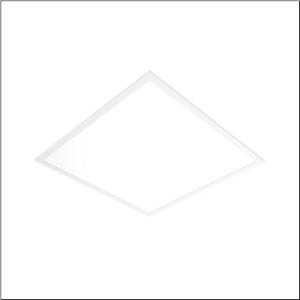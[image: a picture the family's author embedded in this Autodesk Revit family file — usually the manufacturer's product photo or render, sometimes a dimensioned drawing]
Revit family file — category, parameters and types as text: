
# Revit family: apollon_r__41_51mh11w72343_11b4
name_source: partatom
category: Lighting Fixtures
units: mm (PartAtom-declared; Revit-internal decimal feet)

## family parameters
Cut with Voids When Loaded = No
Host = Face
Light Source = No
Part Type = Normal
Room Calculation Point = No
Round Connector Dimension = Use Diameter
Shared = No

## types (1)
- Apollon® 41 (1 x LED, 3500 lm, 28.5 W, 3000K)
    Apparent Load = 29 VA
    CIE Flux Codes = 61 87 97 100 100
    Color Rendering = 80
    Color Temperature = 3000K
    Default Elevation = 1800 mm
    Description = Apollon® 41, office luminaire, primary optical cover: prismatic diffuser, of PS, light emission: direct distribution, primary light characteristic: symmetric, installation type: lay-in mounting, LED, rated luminous flux: 3.500lm, luminous efficacy: 123lm/W, light colour: 830, colour temperature: 3000K, with terminal, 3-pole, mains connection: 220..240V, AC, 50/60Hz, housing, of aluminium section, traffic white (RAL 9016), module: M625, length: 620mm, width: 620mm, height: 40mm, housing upper side, of sheet steel, protection rating (complete): IP20, protection rating (lamp compartment, on room side): IP40, insulation class (complete): insulation class II (safety insulation), certification: CE, ENEC, permissible operating ambient temperature: -20..+40°C, packaging unit: 1 piece
    Height = 0 mm  [stored 0 ft]
    Lamp = 1 x LED
    Lamp Light Flux = 3500 lm
    Lamp Power = 28.5 W
    Lamp count = 1
    Length = 620 mm
    Luminous efficacy = 123 lm/W
    Manufacturer = Siteco
    ModVariant = No
    Model = 51MH11W72343
    Mounting Place = Ceiling
    Mounting Type = Recessed
    Number of Poles = 1
    OnlyDefault = Yes
    Power Factor = 1
    Product Name = Apollon® 41
    Product group = office luminaire | ceiling recessed
    ProductGroupID = 400
    Protection Class = Protection class II
    Protection Degree = IP 20
    RLX_Detail_Level = 1
    RLX_Emergency_Light_Flux = 0 lm
    RLX_Emergency_Type = 0
    RLX_Emergency_Type_DB = No
    RlxData = <blob elided: 12173 chars, md5=02ad86a8>
    Socket = socket
    Standby Power = 0 W
    System Light Flux = 3500 lm
    System Power = 29 W
    Type Comments = Product without accessories
    Type Image = l_1291024.jpg
    URL = http://relux.com
    VarID = ---
    Voltage = 0 V
    Weight = 0.00 kg
    Width = 620 mm

note: [stored X ft] marks values corroborated as IEEE doubles in the binary element streams (Revit-internal decimal feet)

## geometry (parser evidence)
native form markers: Sweep x10
no freeform markers — native parametric forms only
